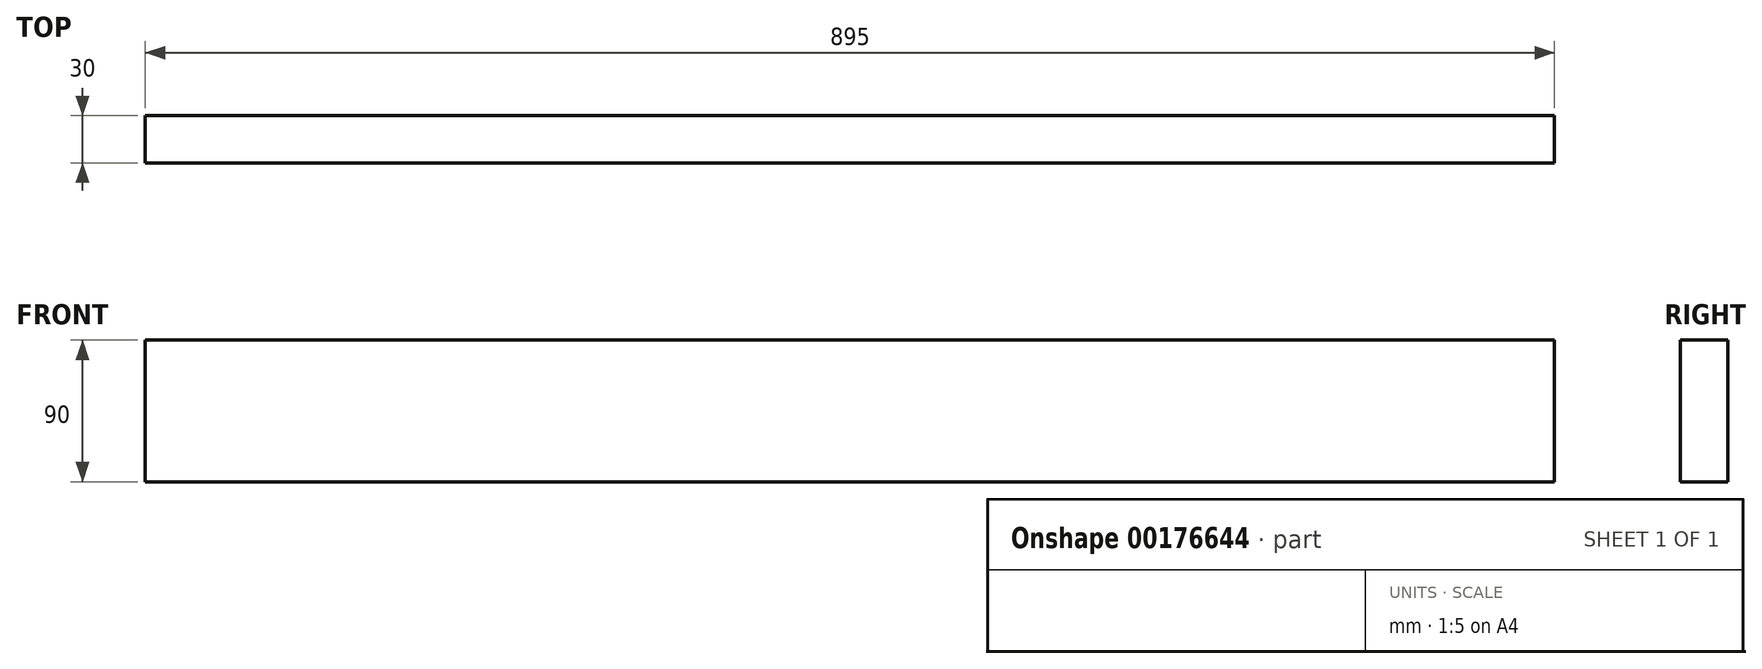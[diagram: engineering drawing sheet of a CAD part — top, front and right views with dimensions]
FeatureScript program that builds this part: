
annotation { "Feature Type Name" : "Feature", "Feature Type Description" : "" }
export const myFeature = defineFeature(function(context is Context, id is Id, definition is map)
    precondition{}
    {
        {
            var Q0;
            Q0=qCreatedBy(makeId("Top.planeOp"),FACE);
            var sketch = newSketch(context, id + "F0", { "sketchPlane" : qUnion([Q0])});
            skLineSegment(sketch, "E0.bottom", {"start": v(447.5, -15) * mm, "end": v(-447.5, -15) * mm});
            skLineSegment(sketch, "E0.top", {"start": v(447.5, 15) * mm, "end": v(-447.5, 15) * mm});
            skLineSegment(sketch, "E0.left", {"start": v(447.5, -15) * mm, "end": v(447.5, 15) * mm});
            skLineSegment(sketch, "E0.right", {"start": v(-447.5, -15) * mm, "end": v(-447.5, 15) * mm});
            skPoint(sketch, "E0.middle", {"position": v(0, 0) * mm});
            skSolve(sketch);
        }
        {
            var Q0;
            Q0=qSketchRegion(id+"F0",true);
            extrude(context, id + "F1", {"entities" : qUnion([Q0]), "depth" : 90 * mm});
        }
    });
